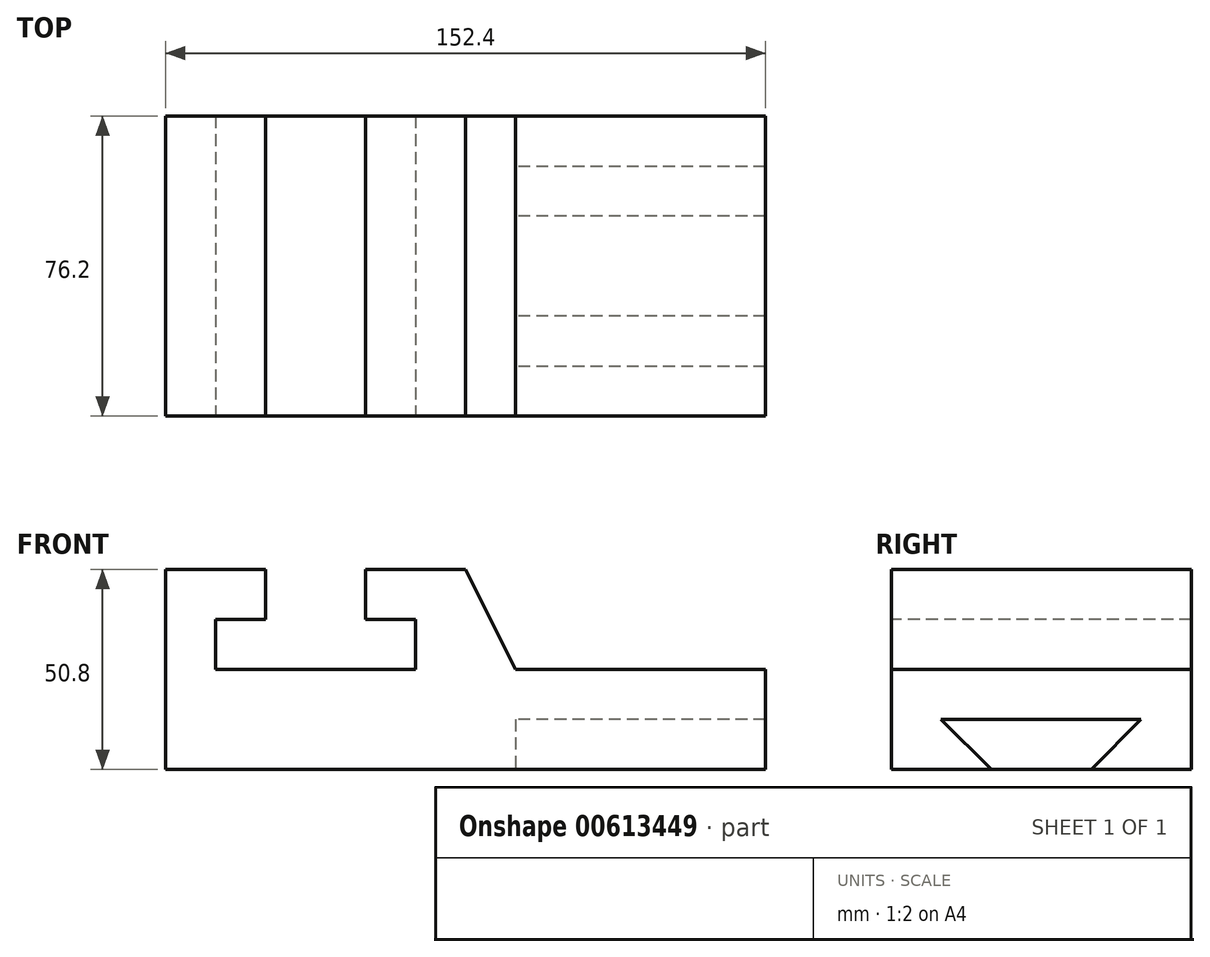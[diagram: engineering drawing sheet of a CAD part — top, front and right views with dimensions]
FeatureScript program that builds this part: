
annotation { "Feature Type Name" : "Feature", "Feature Type Description" : "" }
export const myFeature = defineFeature(function(context is Context, id is Id, definition is map)
    precondition{}
    {
        {
            var Q0;
            Q0=qCreatedBy(makeId("Front.planeOp"),FACE);
            var sketch = newSketch(context, id + "F0", { "sketchPlane" : qUnion([Q0])});
            skLineSegment(sketch, "E0", {"start": v(-88.9, 0) * mm, "end": v(-88.9, 50.8) * mm});
            skLineSegment(sketch, "E1", {"start": v(-88.9, 50.8) * mm, "end": v(-63.5, 50.8) * mm});
            skLineSegment(sketch, "E2", {"start": v(-63.5, 50.8) * mm, "end": v(-63.5, 38.1) * mm});
            skLineSegment(sketch, "E3", {"start": v(-63.5, 38.1) * mm, "end": v(-76.2, 38.1) * mm});
            skLineSegment(sketch, "E4", {"start": v(-76.2, 38.1) * mm, "end": v(-76.2, 25.4) * mm});
            skLineSegment(sketch, "E5", {"start": v(-76.2, 25.4) * mm, "end": v(-25.4, 25.4) * mm});
            skLineSegment(sketch, "E6", {"start": v(-25.4, 25.4) * mm, "end": v(-25.4, 38.1) * mm});
            skLineSegment(sketch, "E7", {"start": v(-25.4, 38.1) * mm, "end": v(-38.1, 38.1) * mm});
            skLineSegment(sketch, "E8", {"start": v(-38.1, 38.1) * mm, "end": v(-38.1, 50.8) * mm});
            skLineSegment(sketch, "E9", {"start": v(-38.1, 50.8) * mm, "end": v(-12.7, 50.8) * mm});
            skLineSegment(sketch, "E10", {"start": v(63.5, 0) * mm, "end": v(63.5, 25.4) * mm});
            skLineSegment(sketch, "E11", {"start": v(63.5, 25.4) * mm, "end": v(0, 25.4) * mm});
            skLineSegment(sketch, "E12", {"start": v(-88.9, 0) * mm, "end": v(63.5, 0) * mm});
            skLineSegment(sketch, "E13", {"start": v(-12.7, 50.8) * mm, "end": v(0, 25.4) * mm});
            skSolve(sketch);
        }
        {
            var Q0;
            Q0=makeQuery(id+"F0.imprint","IMPRINT",FACE,{"disambiguationData":[TD([[makeQuery(id+"F0.imprint","IMPRINT",EDGE,{"derivedFrom":sQuery(id+"F0.wireOp",EDGE,"E0")}),-1.0]])]});
            extrude(context, id + "F1", {"entities" : qUnion([Q0]), "oppositeDirection" : true, "depth" : 76.2 * mm, "offsetDistance" : 25.4 * mm});
        }
        {
            var Q0;
            Q0=qCreatedBy(makeId("Right.planeOp"),FACE);
            var sketch = newSketch(context, id + "F2", { "sketchPlane" : qUnion([Q0])});
            skLineSegment(sketch, "E14", {"start": v(12.63, 12.7) * mm, "end": v(63.43, 12.7) * mm});
            skLineSegment(sketch, "E15", {"start": v(25.4, 0) * mm, "end": v(50.8, 0) * mm});
            skLineSegment(sketch, "E16", {"start": v(12.63, 12.7) * mm, "end": v(25.4, 0) * mm});
            skLineSegment(sketch, "E17", {"start": v(63.43, 12.7) * mm, "end": v(50.8, 0) * mm});
            skSolve(sketch);
        }
        {
            var Q0;
            Q0 = qSketchRegion(id + "F2", true);
            extrude(context, id + "F3", {"entities" : qUnion([Q0]), "operationType" : NewBodyOperationType.REMOVE, "depth" : 203.2 * mm, "offsetDistance" : 25.4 * mm});
        }
    });
